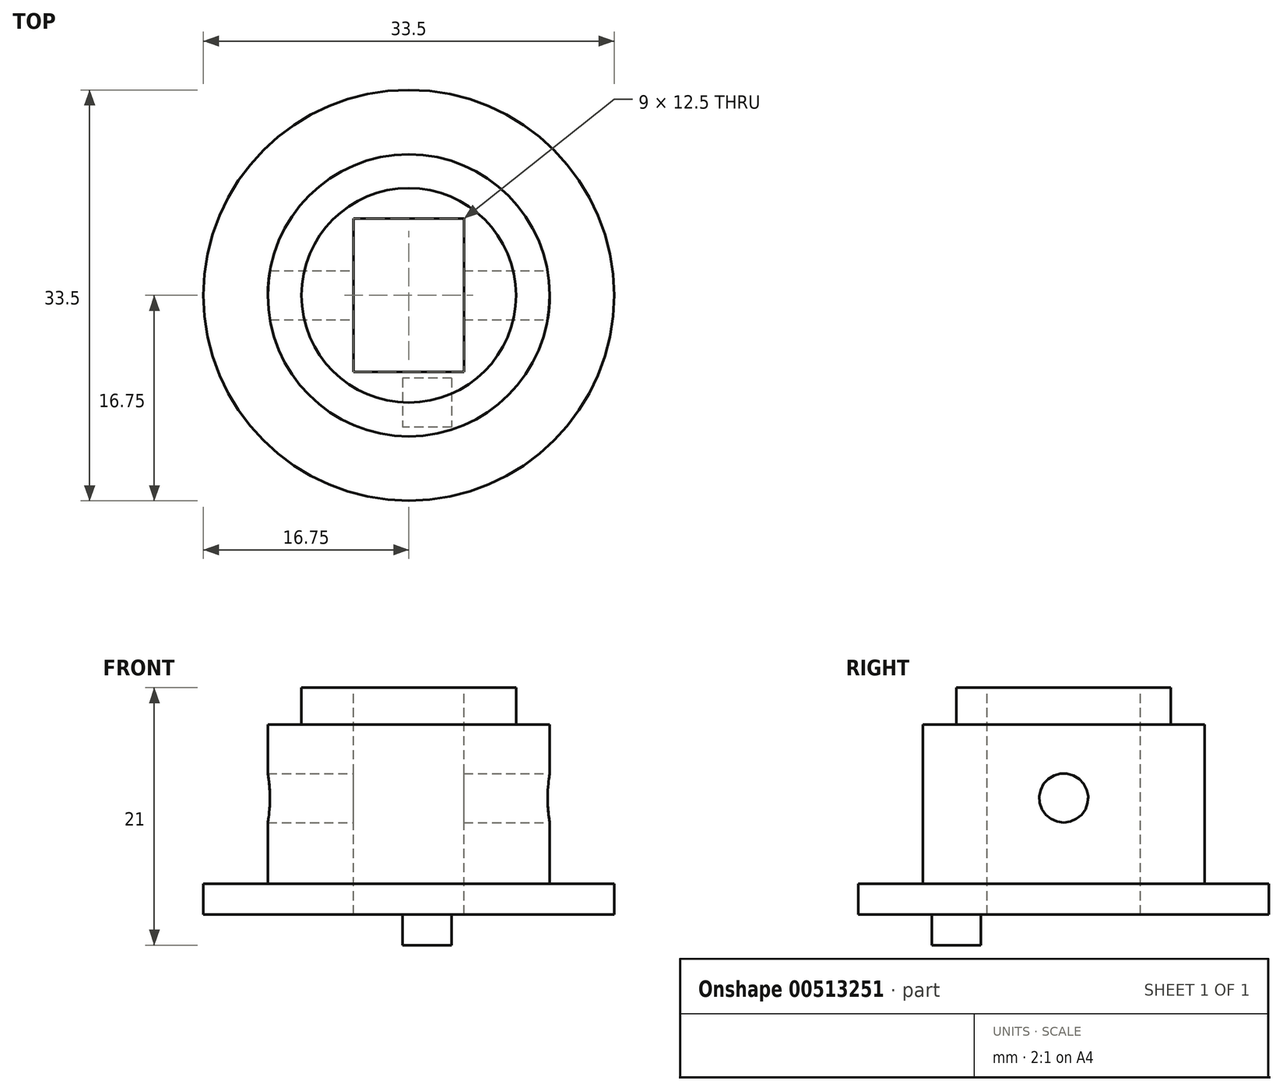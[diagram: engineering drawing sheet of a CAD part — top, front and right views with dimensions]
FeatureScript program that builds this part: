
annotation { "Feature Type Name" : "Feature", "Feature Type Description" : "" }
export const myFeature = defineFeature(function(context is Context, id is Id, definition is map)
    precondition{}
    {
        {
            var Q0;
            Q0=qCreatedBy(makeId("Front.planeOp"),FACE);
            var sketch = newSketch(context, id + "F0", { "sketchPlane" : qUnion([Q0])});
            skLineSegment(sketch, "E0", {"start": v(0, 0) * mm, "end": v(0, 89.94) * mm, "construction": true});
            skLineSegment(sketch, "E1", {"start": v(0, 0) * mm, "end": v(16.75, 0) * mm});
            skLineSegment(sketch, "E2", {"start": v(16.75, 0) * mm, "end": v(16.75, 2.5) * mm});
            skLineSegment(sketch, "E3", {"start": v(16.75, 2.5) * mm, "end": v(11.5, 2.5) * mm});
            skLineSegment(sketch, "E4", {"start": v(11.5, 2.5) * mm, "end": v(11.5, 15.5) * mm});
            skLineSegment(sketch, "E5", {"start": v(11.5, 15.5) * mm, "end": v(8.75, 15.5) * mm});
            skLineSegment(sketch, "E6", {"start": v(8.75, 15.5) * mm, "end": v(8.75, 18.5) * mm});
            skLineSegment(sketch, "E7", {"start": v(8.75, 18.5) * mm, "end": v(0, 18.5) * mm});
            skLineSegment(sketch, "E8", {"start": v(0, 18.5) * mm, "end": v(0, 0) * mm});
            skSolve(sketch);
        }
        {
            var Q0;
            Q0=makeQuery(id+"F0.imprint","IMPRINT",FACE,{"disambiguationData":[TD([[makeQuery(id+"F0.imprint","IMPRINT",EDGE,{"derivedFrom":sQuery(id+"F0.wireOp",EDGE,"E1")}),1.0]])]});
            var Q1;
            Q1=sQuery(id+"F0.wireOp",EDGE,"E0");
            revolve(context, id + "F1", {"entities" : qUnion([Q0]), "axis" : qUnion([Q1]), "revolveType" : RevolveType.FULL});
        }
        {
            var Q0;
            Q0=makeQuery(id+"F1.opRevolve","SWEPT_FACE",FACE,{"disambiguationData":[OSD([sQuery(id+"F0.wireOp",EDGE,"E7")])]});
            var sketch = newSketch(context, id + "F2", { "sketchPlane" : qUnion([Q0])});
            skLineSegment(sketch, "E9.bottom", {"start": v(4.5, -6.25) * mm, "end": v(-4.5, -6.25) * mm});
            skLineSegment(sketch, "E9.top", {"start": v(4.5, 6.25) * mm, "end": v(-4.5, 6.25) * mm});
            skLineSegment(sketch, "E9.left", {"start": v(4.5, -6.25) * mm, "end": v(4.5, 6.25) * mm});
            skLineSegment(sketch, "E9.right", {"start": v(-4.5, -6.25) * mm, "end": v(-4.5, 6.25) * mm});
            skPoint(sketch, "E9.middle", {"position": v(0, 0) * mm});
            skSolve(sketch);
        }
        {
            var Q0;
            Q0 = qSketchRegion(id + "F2", true);
            extrude(context, id + "F3", {"entities" : qUnion([Q0]), "operationType" : NewBodyOperationType.REMOVE, "endBound" : BoundingType.UP_TO_NEXT, "oppositeDirection" : true, "depth" : 25 * mm});
        }
        {
            var Q0;
            Q0=makeQuery(id+"F1.opRevolve","SWEPT_FACE",FACE,{"disambiguationData":[OSD([sQuery(id+"F0.wireOp",EDGE,"E1")])]});
            var sketch = newSketch(context, id + "F4", { "sketchPlane" : qUnion([Q0])});
            skPoint(sketch, "E10.middle", {"position": v(0, 0) * mm});
            skLineSegment(sketch, "E11.bottom", {"start": v(3.5, 6.75) * mm, "end": v(-0.5, 6.75) * mm});
            skLineSegment(sketch, "E11.top", {"start": v(3.5, 10.75) * mm, "end": v(-0.5, 10.75) * mm});
            skLineSegment(sketch, "E11.left", {"start": v(3.5, 6.75) * mm, "end": v(3.5, 10.75) * mm});
            skLineSegment(sketch, "E11.right", {"start": v(-0.5, 6.75) * mm, "end": v(-0.5, 10.75) * mm});
            skSolve(sketch);
        }
        {
            var Q0;
            Q0 = qSketchRegion(id + "F4", true);
            extrude(context, id + "F5", {"entities" : qUnion([Q0]), "operationType" : NewBodyOperationType.ADD, "depth" : 2.5 * mm, "offsetDistance" : 25 * mm});
        }
        {
            var Q0;
            Q0=qCreatedBy(makeId("Right.planeOp"),FACE);
            var sketch = newSketch(context, id + "F6", { "sketchPlane" : qUnion([Q0])});
            skCircle(sketch, "E12", {"center": v(0, 9.5) * mm, "radius": 2 * mm});
            skSolve(sketch);
        }
        {
            var Q0;
            Q0 = qSketchRegion(id + "F6", true);
            extrude(context, id + "F7", {"entities" : qUnion([Q0]), "operationType" : NewBodyOperationType.REMOVE, "endBound" : BoundingType.THROUGH_ALL, "oppositeDirection" : true, "depth" : 25 * mm, "offsetDistance" : 25 * mm, "hasSecondDirection" : true, "secondDirectionBound" : SecondDirectionBoundingType.THROUGH_ALL, "secondDirectionOppositeDirection" : false, "secondDirectionDepth" : 25 * mm});
        }
    });
